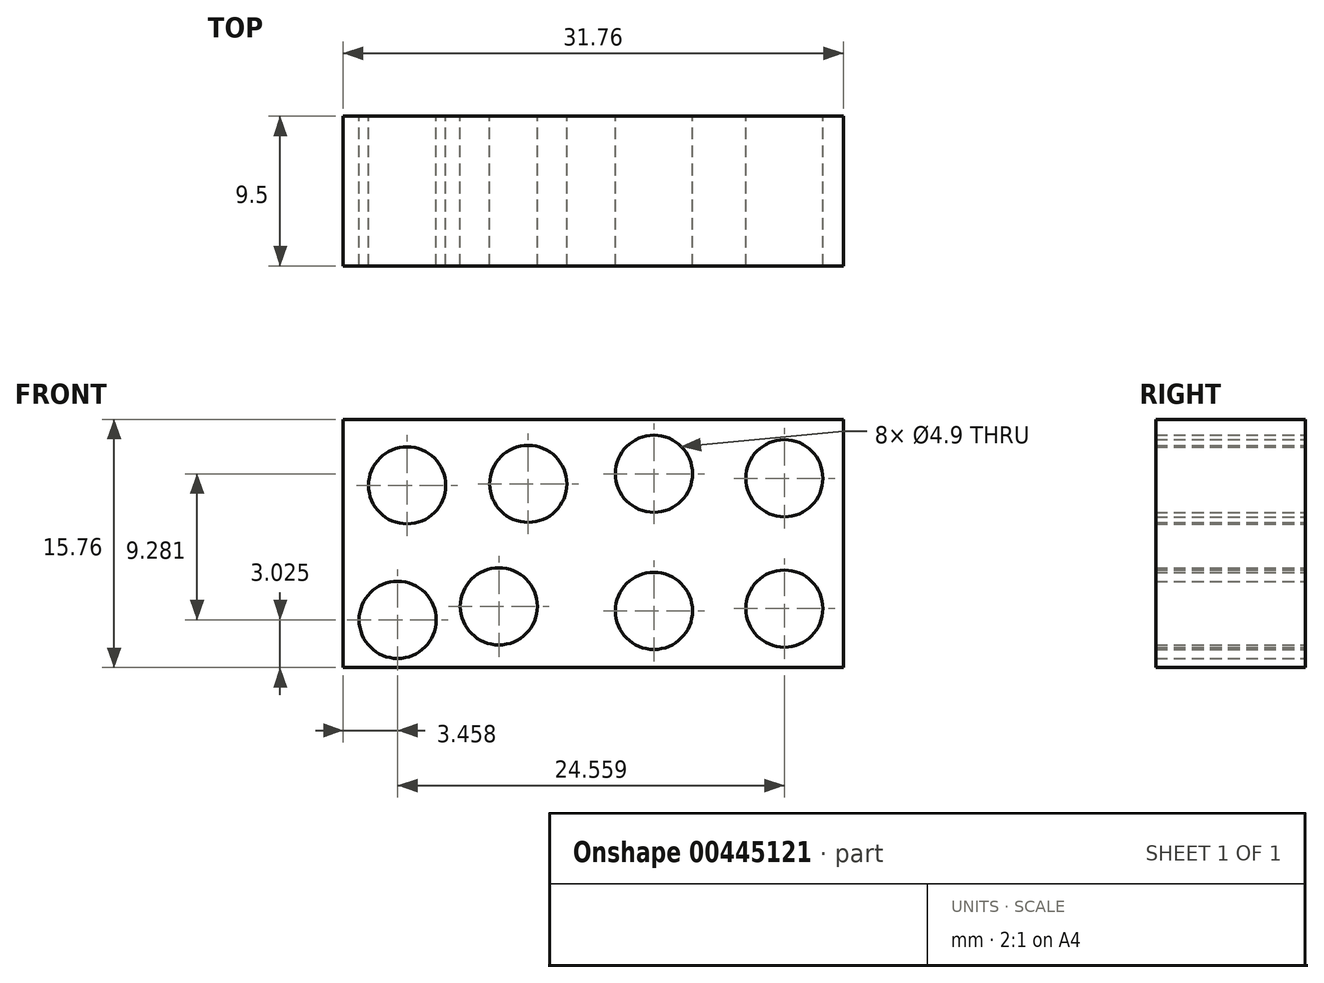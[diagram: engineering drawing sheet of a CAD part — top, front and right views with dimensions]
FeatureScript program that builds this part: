
annotation { "Feature Type Name" : "Feature", "Feature Type Description" : "" }
export const myFeature = defineFeature(function(context is Context, id is Id, definition is map)
    precondition{}
    {
        {
            var Q0;
            Q0=qCreatedBy(makeId("Front.planeOp"),FACE);
            var sketch = newSketch(context, id + "F0", { "sketchPlane" : qUnion([Q0])});
            skLineSegment(sketch, "E0.bottom", {"start": v(15.88, 7.87) * mm, "end": v(-15.88, 7.87) * mm});
            skLineSegment(sketch, "E0.top", {"start": v(15.88, -7.88) * mm, "end": v(-15.88, -7.88) * mm});
            skLineSegment(sketch, "E0.left", {"start": v(15.88, 7.87) * mm, "end": v(15.88, -7.88) * mm});
            skLineSegment(sketch, "E0.right", {"start": v(-15.88, 7.87) * mm, "end": v(-15.88, -7.88) * mm});
            skPoint(sketch, "E0.middle", {"position": v(0, 0) * mm});
            skCircle(sketch, "E1", {"center": v(-11.82, 3.69) * mm, "radius": 2.45 * mm});
            skCircle(sketch, "E2", {"center": v(-4.13, 3.79) * mm, "radius": 2.45 * mm});
            skCircle(sketch, "E3", {"center": v(3.86, 4.43) * mm, "radius": 2.45 * mm});
            skCircle(sketch, "E4", {"center": v(12.14, 4.14) * mm, "radius": 2.45 * mm});
            skCircle(sketch, "E5", {"center": v(-12.42, -4.85) * mm, "radius": 2.45 * mm});
            skCircle(sketch, "E6", {"center": v(-6, -4) * mm, "radius": 2.45 * mm});
            skCircle(sketch, "E7", {"center": v(3.86, -4.28) * mm, "radius": 2.45 * mm});
            skCircle(sketch, "E8", {"center": v(12.14, -4.14) * mm, "radius": 2.45 * mm});
            skSolve(sketch);
        }
        {
            var Q0;
            Q0=makeQuery(id+"F0.imprint","IMPRINT",FACE,{"disambiguationData":[TD([[makeQuery(id+"F0.imprint","IMPRINT",EDGE,{"derivedFrom":sQuery(id+"F0.wireOp",EDGE,"E0.bottom")}),1.0]])]});
            extrude(context, id + "F1", {"entities" : qUnion([Q0]), "depth" : 9.5 * mm});
        }
    });
